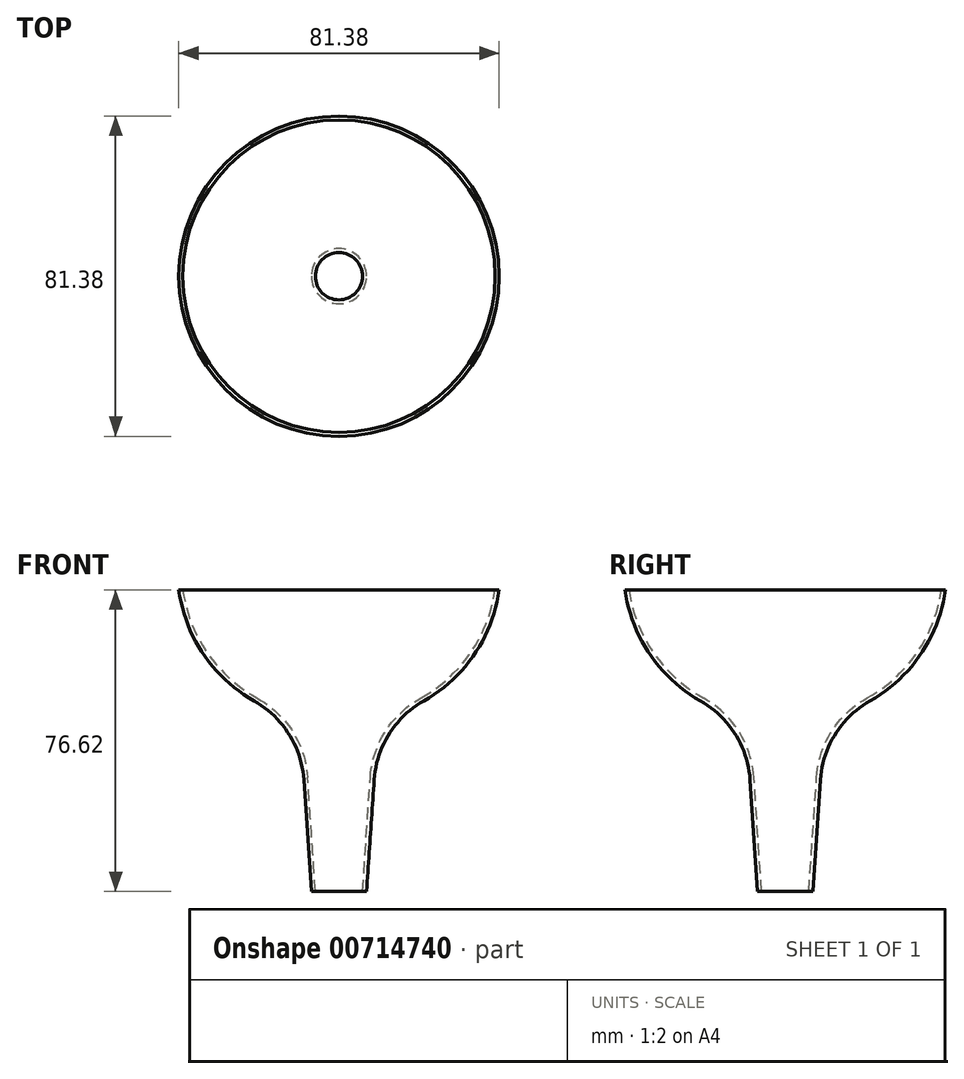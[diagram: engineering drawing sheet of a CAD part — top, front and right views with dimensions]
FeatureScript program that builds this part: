
annotation { "Feature Type Name" : "Feature", "Feature Type Description" : "" }
export const myFeature = defineFeature(function(context is Context, id is Id, definition is map)
    precondition{}
    {
        {
            var Q0;
            Q0=qCreatedBy(makeId("Right.planeOp"),FACE);
            var sketch = newSketch(context, id + "F0", { "sketchPlane" : qUnion([Q0])});
            skLineSegment(sketch, "E0", {"start": v(0, 0) * mm, "end": v(0, 74.56) * mm, "construction": true});
            skLineSegment(sketch, "E1", {"start": v(6, 0) * mm, "end": v(9.05, 45) * mm});
            skArc(sketch, "E2", {"start": v(9.05, 45) * mm, "mid": v(29.52, 55.82) * mm, "end": v(39.68, 76.62) * mm});
            skArc(sketch, "E3.0", {"start": v(10, 44.16) * mm, "mid": v(30.56, 55.46) * mm, "end": v(40.7, 76.62) * mm});
            skLineSegment(sketch, "E3.1", {"start": v(7, 0) * mm, "end": v(10, 44.16) * mm});
            skLineSegment(sketch, "E4", {"start": v(39.68, 76.62) * mm, "end": v(40.7, 76.62) * mm});
            skLineSegment(sketch, "E5", {"start": v(6, 0) * mm, "end": v(7, 0) * mm});
            skSolve(sketch);
        }
        {
            var Q0;
            Q0 = qSketchRegion(id + "F0", true);
            var Q1;
            Q1=sQuery(id+"F0.wireOp",EDGE,"E0");
            revolve(context, id + "F1", {"surfaceOperationType" : NewSurfaceOperationType.NEW, "entities" : qUnion([Q0]), "axis" : qUnion([Q1]), "revolveType" : RevolveType.FULL});
        }
        {
            var Q0;
            Q0=makeQuery(id+"F1.opRevolve","SWEPT_EDGE",EDGE,{"disambiguationData":[OSD([sQuery(id+"F0.wireOp",EDGE,"E3.0"),sQuery(id+"F0.wireOp",EDGE,"E3.1")])]});
            var Q1;
            Q1=makeQuery(id+"F1.opRevolve","SWEPT_EDGE",EDGE,{"disambiguationData":[OSD([sQuery(id+"F0.wireOp",EDGE,"E1"),sQuery(id+"F0.wireOp",EDGE,"E2")])]});
            fillet(context, id + "F2", {"entities" : qUnion([Q0, Q1]), "radius" : 25 * mm, "tangentPropagation" : true, "allowEdgeOverflow" : false});
        }
    });
